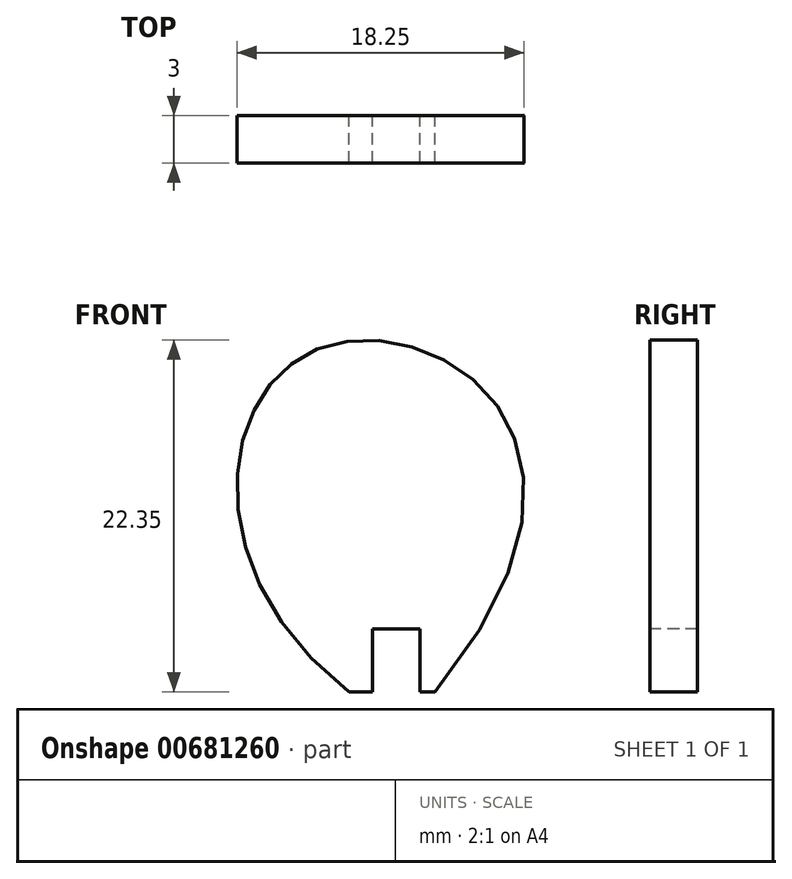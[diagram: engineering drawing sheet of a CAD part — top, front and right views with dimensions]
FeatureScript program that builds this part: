
annotation { "Feature Type Name" : "Feature", "Feature Type Description" : "" }
export const myFeature = defineFeature(function(context is Context, id is Id, definition is map)
    precondition{}
    {
        {
            assignVariable(context, id + "F0", {"name" : "MaterialDepth", "anyValue" : 3 * mm});
        }
        {
            var Q0;
            Q0=qCreatedBy(makeId("Front.planeOp"),FACE);
            var sketch = newSketch(context, id + "F1", { "sketchPlane" : qUnion([Q0])});
            skLineSegment(sketch, "E0", {"start": v(0, 53.6) * mm, "end": v(0, -7.3) * mm, "construction": true});
            skFitSpline(sketch, "E1", {"points": [v(-3, 0) * mm, v(-4.34, 22) * mm, v(2.48, 0) * mm], "startDerivative": vector(-61.56, 47.6) * mm, "endDerivative": vector(-77.49, -94.85) * mm});
            skLineSegment(sketch, "E2", {"start": v(-3, 0) * mm, "end": v(2.48, 0) * mm});
            skSolve(sketch);
        }
        {
            var Q0;
            Q0=makeQuery(id+"F1.imprint","IMPRINT",FACE,{"disambiguationData":[TD([[makeQuery(id+"F1.imprint","IMPRINT",EDGE,{"derivedFrom":sQuery(id+"F1.wireOp",EDGE,"E1")}),-1.0]])]});
            extrude(context, id + "F2", {"entities" : qUnion([Q0]), "endBound" : BoundingType.SYMMETRIC, "depth" : getVariable(context, 'MaterialDepth'), "offsetDistance" : 25 * mm});
        }
        {
            var Q0;
            Q0=makeQuery(id+"F2.opExtrude","CAP_FACE",FACE,{"disambiguationData":[OSD([sQuery(id+"F1.wireOp",EDGE,"E1"),sQuery(id+"F1.wireOp",EDGE,"E2")])],"isStart":false});
            var sketch = newSketch(context, id + "F3", { "sketchPlane" : qUnion([Q0])});
            skLineSegment(sketch, "E3.bottom", {"start": v(1.5, -4) * mm, "end": v(-1.5, -4) * mm});
            skLineSegment(sketch, "E3.top", {"start": v(1.5, 4) * mm, "end": v(-1.5, 4) * mm});
            skLineSegment(sketch, "E3.left", {"start": v(1.5, -4) * mm, "end": v(1.5, 4) * mm});
            skLineSegment(sketch, "E3.right", {"start": v(-1.5, -4) * mm, "end": v(-1.5, 4) * mm});
            skPoint(sketch, "E3.middle", {"position": v(0, 0) * mm});
            skSolve(sketch);
        }
        {
            var Q0;
            Q0=qSketchRegion(id+"F3",true);
            extrude(context, id + "F4", {"entities" : qUnion([Q0]), "operationType" : NewBodyOperationType.REMOVE, "oppositeDirection" : true, "depth" : 25 * mm, "offsetDistance" : 25 * mm});
        }
    });
